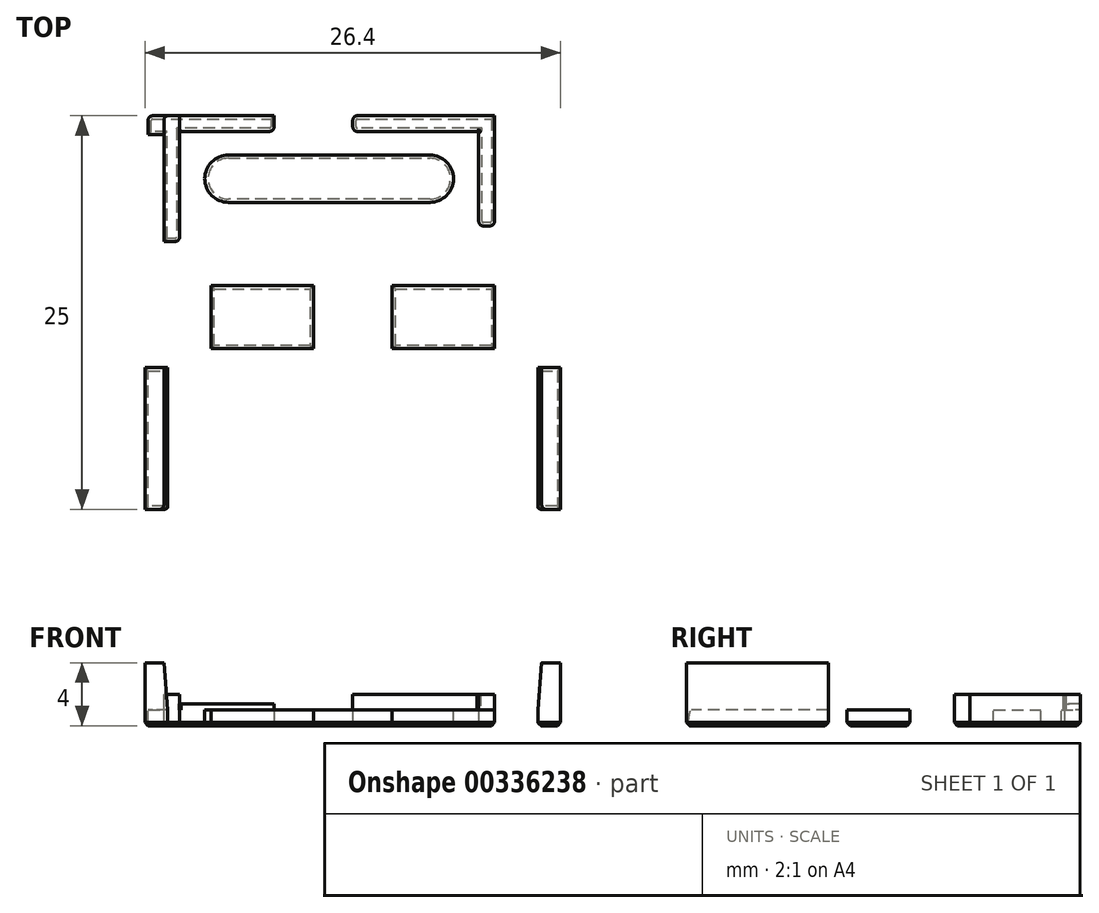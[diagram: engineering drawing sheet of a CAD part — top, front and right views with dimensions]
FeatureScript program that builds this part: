
annotation { "Feature Type Name" : "Feature", "Feature Type Description" : "" }
export const myFeature = defineFeature(function(context is Context, id is Id, definition is map)
    precondition{}
    {
        {
            var Q0;
            Q0=qCreatedBy(makeId("Top.planeOp"),FACE);
            var sketch = newSketch(context, id + "F0", { "sketchPlane" : qUnion([Q0])});
            skLineSegment(sketch, "E0.bottom", {"start": v(12, 8) * mm, "end": v(-12, 8) * mm, "construction": true});
            skLineSegment(sketch, "E0.top", {"start": v(12, -8) * mm, "end": v(-12, -8) * mm});
            skLineSegment(sketch, "E0.left", {"start": v(12, 8) * mm, "end": v(12, -8) * mm});
            skLineSegment(sketch, "E0.right", {"start": v(-12, 8) * mm, "end": v(-12, -8) * mm});
            skPoint(sketch, "E0.middle", {"position": v(0, 0) * mm});
            skLineSegment(sketch, "E1.bottom", {"start": v(-12, -8) * mm, "end": v(-13.2, -8) * mm});
            skLineSegment(sketch, "E1.top", {"start": v(-12, 1) * mm, "end": v(-13.2, 1) * mm});
            skLineSegment(sketch, "E1.right", {"start": v(-13.2, -8) * mm, "end": v(-13.2, 1) * mm});
            skLineSegment(sketch, "E2.bottom", {"start": v(12, -8) * mm, "end": v(13.2, -8) * mm});
            skLineSegment(sketch, "E2.top", {"start": v(12, 1) * mm, "end": v(13.2, 1) * mm});
            skLineSegment(sketch, "E2.right", {"start": v(13.2, -8) * mm, "end": v(13.2, 1) * mm});
            skLineSegment(sketch, "E3", {"start": v(-12, 8) * mm, "end": v(-12, 9) * mm});
            skLineSegment(sketch, "E4", {"start": v(-12, 9) * mm, "end": v(12, 9) * mm, "construction": true});
            skLineSegment(sketch, "E5", {"start": v(12, 9) * mm, "end": v(12, 8) * mm});
            skLineSegment(sketch, "E6", {"start": v(-12, 9) * mm, "end": v(-12, 17) * mm});
            skLineSegment(sketch, "E7", {"start": v(-12, 17) * mm, "end": v(12, 17) * mm});
            skLineSegment(sketch, "E8", {"start": v(12, 17) * mm, "end": v(12, 9) * mm});
            skSolve(sketch);
        }
        {
            var Q0;
            Q0=qCreatedBy(makeId("Front.planeOp"),FACE);
            var sketch = newSketch(context, id + "F1", { "sketchPlane" : qUnion([Q0])});
            skLineSegment(sketch, "E9", {"start": v(0, 0) * mm, "end": v(0, 1) * mm});
            skLineSegment(sketch, "E10", {"start": v(0, 1) * mm, "end": v(0, 4) * mm});
            skSolve(sketch);
        }
        {
            var Q0;
            {var subQ4=sQuery(id+"F0.wireOp",EDGE,"E0.top");Q0=makeQuery(id+"F0.imprint","IMPRINT",FACE,{"disambiguationData":[TD([[makeQuery(id+"F0.imprint","IMPRINT",EDGE,{"derivedFrom":subQ4}),-1.0]])]});}
            var Q1;
            {var subQ0=sQuery(id+"F0.wireOp",EDGE,"E1.bottom");Q1=makeQuery(id+"F0.imprint","IMPRINT",FACE,{"disambiguationData":[TD([[makeQuery(id+"F0.imprint","IMPRINT",EDGE,{"derivedFrom":subQ0}),-1.0]])]});}
            var Q2;
            {var subQ0=sQuery(id+"F0.wireOp",EDGE,"E2.bottom");Q2=makeQuery(id+"F0.imprint","IMPRINT",FACE,{"disambiguationData":[TD([[makeQuery(id+"F0.imprint","IMPRINT",EDGE,{"derivedFrom":subQ0}),1.0]])]});}
            var Q3;
            Q3=sQuery(id+"F1.wireOp",EDGE,"E9");
            sweep(context, id + "F2", {"profiles" : qUnion([Q0, Q1, Q2]), "path" : qUnion([Q3])});
        }
        {
            var Q0;
            {var subQ0=sQuery(id+"F0.wireOp",EDGE,"E1.bottom");Q0=makeQuery(id+"F0.imprint","IMPRINT",FACE,{"disambiguationData":[TD([[makeQuery(id+"F0.imprint","IMPRINT",EDGE,{"derivedFrom":subQ0}),-1.0]])]});}
            var Q1;
            {var subQ0=sQuery(id+"F0.wireOp",EDGE,"E2.bottom");Q1=makeQuery(id+"F0.imprint","IMPRINT",FACE,{"disambiguationData":[TD([[makeQuery(id+"F0.imprint","IMPRINT",EDGE,{"derivedFrom":subQ0}),1.0]])]});}
            var Q2;
            Q2=sQuery(id+"F1.wireOp",EDGE,"E9");
            var Q3;
            Q3=sQuery(id+"F1.wireOp",EDGE,"E10");
            sweep(context, id + "F3", {"operationType" : NewBodyOperationType.ADD, "profiles" : qUnion([Q0, Q1]), "path" : qUnion([Q2, Q3])});
        }
        {
            var Q0;
            {var subQ0=sQuery(id+"F1.wireOp",EDGE,"E9");var subQ1=sQuery(id+"F0.wireOp",EDGE,"E2.bottom");var subQ2=sQuery(id+"F0.wireOp",EDGE,"E1.bottom");Q0=makeQuery(id+"F3.boolean.opBoolean","MERGE",FACE,{"derivedFrom":[makeQuery(id+"F2.opSweep","SWEPT_FACE",FACE,{"disambiguationData":[OSD([sQuery(id+"F0.wireOp",EDGE,"E0.top"),subQ2,subQ1,subQ0])]}),makeQuery(id+"F3.opSweep","SWEPT_FACE",FACE,{"disambiguationData":[OSD([subQ2,subQ0])]}),makeQuery(id+"F3.opSweep","SWEPT_FACE",FACE,{"disambiguationData":[OSD([subQ1,subQ0])]})]});}
            var sketch = newSketch(context, id + "F4", { "sketchPlane" : qUnion([Q0])});
            skLineSegment(sketch, "E11", {"start": v(-12, 4) * mm, "end": v(-11.75, 1) * mm});
            skLineSegment(sketch, "E12", {"start": v(-11.75, 1) * mm, "end": v(-12, 1) * mm});
            skLineSegment(sketch, "E13", {"start": v(-12, 1) * mm, "end": v(-12, 4) * mm});
            skLineSegment(sketch, "E14.MirrorCS", {"start": v(12, 4) * mm, "end": v(11.75, 1) * mm});
            skLineSegment(sketch, "E15.MirrorCS", {"start": v(12, 1) * mm, "end": v(12, 4) * mm});
            skLineSegment(sketch, "E16.MirrorCS", {"start": v(11.75, 1) * mm, "end": v(12, 1) * mm});
            skSolve(sketch);
        }
        {
            var Q0;
            Q0 = qSketchRegion(id + "F4", true);
            var Q1;
            {var subQ0=sQuery(id+"F1.wireOp",EDGE,"E9");var subQ1=sQuery(id+"F0.wireOp",EDGE,"E1.top");Q1=makeQuery(id+"F3.boolean.opBoolean","MERGE",FACE,{"derivedFrom":[makeQuery(id+"F2.opSweep","SWEPT_FACE",FACE,{"disambiguationData":[OSD([subQ1,subQ0])]}),makeQuery(id+"F3.opSweep","SWEPT_FACE",FACE,{"disambiguationData":[OSD([subQ1,subQ0])]})]});}
            extrude(context, id + "F5", {"entities" : qUnion([Q0]), "operationType" : NewBodyOperationType.ADD, "endBound" : BoundingType.UP_TO_SURFACE, "oppositeDirection" : true, "depth" : 25 * mm, "endBoundEntityFace" : qUnion([Q1]), "offsetDistance" : 25 * mm});
        }
        {
            var Q0;
            Q0=makeQuery(id+"F2.opSweep","CAP_FACE",FACE,{"disambiguationData":[OSD([sQuery(id+"F0.wireOp",EDGE,"E0.top"),sQuery(id+"F0.wireOp",EDGE,"E0.left"),sQuery(id+"F0.wireOp",EDGE,"E0.right"),sQuery(id+"F0.wireOp",EDGE,"E1.bottom"),sQuery(id+"F0.wireOp",EDGE,"E1.top"),sQuery(id+"F0.wireOp",EDGE,"E1.right"),sQuery(id+"F0.wireOp",EDGE,"E2.bottom"),sQuery(id+"F0.wireOp",EDGE,"E2.top"),sQuery(id+"F0.wireOp",EDGE,"E2.right"),sQuery(id+"F0.wireOp",EDGE,"E3"),sQuery(id+"F0.wireOp",EDGE,"E5"),sQuery(id+"F0.wireOp",EDGE,"E6"),sQuery(id+"F0.wireOp",EDGE,"E7"),sQuery(id+"F0.wireOp",EDGE,"E8"),sQuery(id+"F1.wireOp",VERTEX,"E9.end")])],"isStart":false});
            var sketch = newSketch(context, id + "F6", { "sketchPlane" : qUnion([Q0])});
            skLineSegment(sketch, "E17.bottom", {"start": v(-12, 17) * mm, "end": v(-11, 17) * mm});
            skLineSegment(sketch, "E17.top", {"start": v(-12, 9) * mm, "end": v(-11, 9) * mm});
            skLineSegment(sketch, "E17.left", {"start": v(-12, 17) * mm, "end": v(-12, 9) * mm});
            skLineSegment(sketch, "E17.right", {"start": v(-11, 17) * mm, "end": v(-11, 9) * mm});
            skLineSegment(sketch, "E18", {"start": v(0, 17) * mm, "end": v(9, 17) * mm});
            skLineSegment(sketch, "E19", {"start": v(9, 17) * mm, "end": v(9, 10) * mm});
            skLineSegment(sketch, "E20", {"start": v(9, 10) * mm, "end": v(8, 10) * mm});
            skLineSegment(sketch, "E21", {"start": v(8, 10) * mm, "end": v(8, 16) * mm});
            skLineSegment(sketch, "E22", {"start": v(8, 16) * mm, "end": v(0, 16) * mm});
            skLineSegment(sketch, "E23", {"start": v(0, 16) * mm, "end": v(0, 17) * mm});
            skLineSegment(sketch, "E24", {"start": v(-7.9, 13) * mm, "end": v(4.9, 13) * mm, "construction": true});
            skPoint(sketch, "E24.startSnap0", {"position": v(-11, 13) * mm});
            skArc(sketch, "E25.0.startCap", {"start": v(-7.9, 11.5) * mm, "mid": v(-9.4, 13) * mm, "end": v(-7.9, 14.5) * mm});
            skArc(sketch, "E25.0.endCap", {"start": v(4.9, 14.5) * mm, "mid": v(6.4, 13) * mm, "end": v(4.9, 11.5) * mm});
            skLineSegment(sketch, "E25.0.left", {"start": v(-7.9, 14.5) * mm, "end": v(4.9, 14.5) * mm});
            skLineSegment(sketch, "E25.0.right", {"start": v(-7.9, 11.5) * mm, "end": v(4.9, 11.5) * mm});
            skLineSegment(sketch, "E26", {"start": v(8, 10) * mm, "end": v(-11, 10) * mm, "construction": true});
            skArc(sketch, "E27", {"start": v(12, 14.5) * mm, "mid": v(10.5, 13) * mm, "end": v(12, 11.5) * mm});
            skLineSegment(sketch, "E28", {"start": v(12, 14.5) * mm, "end": v(12, 11.5) * mm});
            skLineSegment(sketch, "E29", {"start": v(-12, 17) * mm, "end": v(-13, 17) * mm});
            skLineSegment(sketch, "E30", {"start": v(-13, 17) * mm, "end": v(-13, 15.8) * mm});
            skLineSegment(sketch, "E31", {"start": v(-13, 15.8) * mm, "end": v(-12, 15.8) * mm});
            skLineSegment(sketch, "E32.bottom", {"start": v(-2.5, 6.2) * mm, "end": v(-9, 6.2) * mm});
            skLineSegment(sketch, "E32.top", {"start": v(-2.5, 2.2) * mm, "end": v(-9, 2.2) * mm});
            skLineSegment(sketch, "E32.left", {"start": v(-2.5, 6.2) * mm, "end": v(-2.5, 2.2) * mm});
            skLineSegment(sketch, "E32.right", {"start": v(-9, 6.2) * mm, "end": v(-9, 2.2) * mm});
            skLineSegment(sketch, "E33.MirrorCS", {"start": v(2.5, 6.2) * mm, "end": v(2.5, 2.2) * mm});
            skLineSegment(sketch, "E34.MirrorCS", {"start": v(2.5, 6.2) * mm, "end": v(9, 6.2) * mm});
            skLineSegment(sketch, "E35.MirrorCS", {"start": v(2.5, 2.2) * mm, "end": v(9, 2.2) * mm});
            skLineSegment(sketch, "E36.MirrorCS", {"start": v(9, 6.2) * mm, "end": v(9, 2.2) * mm});
            skLineSegment(sketch, "E37", {"start": v(-11, 17) * mm, "end": v(-5, 17) * mm});
            skLineSegment(sketch, "E38", {"start": v(-5, 17) * mm, "end": v(-5, 16) * mm});
            skLineSegment(sketch, "E39", {"start": v(-5, 16) * mm, "end": v(-11, 16) * mm});
            skSolve(sketch);
        }
        {
            var Q0;
            {var subQ1=sQuery(id+"F6.wireOp",EDGE,"E17.bottom");Q0=makeQuery(id+"F6.imprint","IMPRINT",FACE,{"disambiguationData":[TD([[makeQuery(id+"F6.imprint","IMPRINT",EDGE,{"derivedFrom":subQ1}),1.0]])]});}
            var Q1;
            Q1=makeQuery(id+"F6.imprint","IMPRINT",FACE,{"disambiguationData":[TD([[makeQuery(id+"F6.imprint","IMPRINT",EDGE,{"derivedFrom":sQuery(id+"F6.wireOp",EDGE,"E18")}),1.0]])]});
            extrude(context, id + "F7", {"entities" : qUnion([Q0, Q1]), "operationType" : NewBodyOperationType.ADD, "depth" : 1 * mm, "offsetDistance" : 25 * mm});
        }
        {
            var Q0;
            {var subQ0=sQuery(id+"F6.wireOp",EDGE,"E37");Q0=makeQuery(id+"F6.imprint","IMPRINT",FACE,{"disambiguationData":[TD([[makeQuery(id+"F6.imprint","IMPRINT",EDGE,{"derivedFrom":subQ0}),1.0]])]});}
            extrude(context, id + "F8", {"entities" : qUnion([Q0]), "operationType" : NewBodyOperationType.ADD, "depth" : 0.4 * mm, "offsetDistance" : 25 * mm});
        }
        {
            var Q0;
            Q0=makeQuery(id+"F6.imprint","IMPRINT",FACE,{"disambiguationData":[TD([[makeQuery(id+"F6.imprint","IMPRINT",EDGE,{"derivedFrom":sQuery(id+"F6.wireOp",EDGE,"E25.0.startCap")}),-1.0]])]});
            var Q1;
            Q1=makeQuery(id+"F6.imprint","IMPRINT",FACE,{"disambiguationData":[TD([[makeQuery(id+"F6.imprint","IMPRINT",EDGE,{"derivedFrom":sQuery(id+"F6.wireOp",EDGE,"E27")}),1.0]])]});
            var Q2;
            Q2=makeQuery(id+"F2.opSweep","CAP_FACE",FACE,{"disambiguationData":[OSD([sQuery(id+"F0.wireOp",EDGE,"E0.top"),sQuery(id+"F0.wireOp",EDGE,"E0.left"),sQuery(id+"F0.wireOp",EDGE,"E0.right"),sQuery(id+"F0.wireOp",EDGE,"E1.bottom"),sQuery(id+"F0.wireOp",EDGE,"E1.top"),sQuery(id+"F0.wireOp",EDGE,"E1.right"),sQuery(id+"F0.wireOp",EDGE,"E2.bottom"),sQuery(id+"F0.wireOp",EDGE,"E2.top"),sQuery(id+"F0.wireOp",EDGE,"E2.right"),sQuery(id+"F0.wireOp",EDGE,"E3"),sQuery(id+"F0.wireOp",EDGE,"E5"),sQuery(id+"F0.wireOp",EDGE,"E6"),sQuery(id+"F0.wireOp",EDGE,"E7"),sQuery(id+"F0.wireOp",EDGE,"E8"),sQuery(id+"F1.wireOp",VERTEX,"E9.start")])],"isStart":true});
            extrude(context, id + "F9", {"entities" : qUnion([Q0, Q1]), "operationType" : NewBodyOperationType.REMOVE, "endBound" : BoundingType.UP_TO_SURFACE, "oppositeDirection" : true, "depth" : 25 * mm, "endBoundEntityFace" : qUnion([Q2]), "offsetDistance" : 25 * mm});
        }
        {
            var Q0;
            {var subQ0=sQuery(id+"F6.wireOp",EDGE,"E29");Q0=makeQuery(id+"F6.imprint","IMPRINT",FACE,{"disambiguationData":[TD([[makeQuery(id+"F6.imprint","IMPRINT",EDGE,{"derivedFrom":subQ0}),1.0]])]});}
            var Q1;
            Q1=makeQuery(id+"F2.opSweep","CAP_FACE",FACE,{"disambiguationData":[OSD([sQuery(id+"F0.wireOp",EDGE,"E0.top"),sQuery(id+"F0.wireOp",EDGE,"E0.left"),sQuery(id+"F0.wireOp",EDGE,"E0.right"),sQuery(id+"F0.wireOp",EDGE,"E1.bottom"),sQuery(id+"F0.wireOp",EDGE,"E1.top"),sQuery(id+"F0.wireOp",EDGE,"E1.right"),sQuery(id+"F0.wireOp",EDGE,"E2.bottom"),sQuery(id+"F0.wireOp",EDGE,"E2.top"),sQuery(id+"F0.wireOp",EDGE,"E2.right"),sQuery(id+"F0.wireOp",EDGE,"E3"),sQuery(id+"F0.wireOp",EDGE,"E5"),sQuery(id+"F0.wireOp",EDGE,"E6"),sQuery(id+"F0.wireOp",EDGE,"E7"),sQuery(id+"F0.wireOp",EDGE,"E8"),sQuery(id+"F1.wireOp",VERTEX,"E9.start")])],"isStart":true});
            extrude(context, id + "F10", {"entities" : qUnion([Q0]), "operationType" : NewBodyOperationType.ADD, "endBound" : BoundingType.UP_TO_SURFACE, "oppositeDirection" : true, "depth" : 25 * mm, "endBoundEntityFace" : qUnion([Q1]), "offsetDistance" : 25 * mm});
        }
        {
            var Q0;
            Q0=makeQuery(id+"F5.opExtrude","CAP_EDGE",EDGE,{"disambiguationData":[OSD([sQuery(id+"F4.wireOp",EDGE,"E11")])],"isStart":true});
            var Q1;
            {var subQ0=sQuery(id+"F1.wireOp",EDGE,"E9");var subQ1=sQuery(id+"F0.wireOp",EDGE,"E1.top");Q1=makeQuery(id+"F5.opExtrude","TWEAK_EDGE",EDGE,{"derivedFrom":[makeQuery(id+"F3.boolean.opBoolean","MERGE",FACE,{"derivedFrom":[makeQuery(id+"F2.opSweep","SWEPT_FACE",FACE,{"disambiguationData":[OSD([subQ1,subQ0])]}),makeQuery(id+"F3.opSweep","SWEPT_FACE",FACE,{"disambiguationData":[OSD([subQ1,subQ0])]})]}),makeQuery(id+"F4.imprint","IMPRINT",EDGE,{"derivedFrom":sQuery(id+"F4.wireOp",EDGE,"E11")})]});}
            var Q2;
            {var subQ0=sQuery(id+"F1.wireOp",EDGE,"E9");var subQ1=sQuery(id+"F0.wireOp",EDGE,"E1.top");Q2=makeQuery(id+"F5.opExtrude","TWEAK_EDGE",EDGE,{"derivedFrom":[makeQuery(id+"F3.boolean.opBoolean","MERGE",FACE,{"derivedFrom":[makeQuery(id+"F2.opSweep","SWEPT_FACE",FACE,{"disambiguationData":[OSD([subQ1,subQ0])]}),makeQuery(id+"F3.opSweep","SWEPT_FACE",FACE,{"disambiguationData":[OSD([subQ1,subQ0])]})]}),makeQuery(id+"F4.imprint","IMPRINT",EDGE,{"derivedFrom":sQuery(id+"F4.wireOp",EDGE,"E14.MirrorCS")})]});}
            var Q3;
            Q3=makeQuery(id+"F5.opExtrude","CAP_EDGE",EDGE,{"disambiguationData":[OSD([sQuery(id+"F4.wireOp",EDGE,"E14.MirrorCS")])],"isStart":true});
            var Q4;
            Q4=makeQuery(id+"F7.opExtrude","SWEPT_EDGE",EDGE,{"disambiguationData":[OSD([sQuery(id+"F6.wireOp",EDGE,"E17.top"),sQuery(id+"F6.wireOp",EDGE,"E17.right")])]});
            var Q5;
            Q5=makeQuery(id+"F7.opExtrude","SWEPT_EDGE",EDGE,{"disambiguationData":[OSD([sQuery(id+"F6.wireOp",EDGE,"E22"),sQuery(id+"F6.wireOp",EDGE,"E23")])]});
            var Q6;
            Q6=makeQuery(id+"F7.opExtrude","SWEPT_EDGE",EDGE,{"disambiguationData":[OSD([sQuery(id+"F0.wireOp",EDGE,"E7"),sQuery(id+"F1.wireOp",VERTEX,"E9.end"),sQuery(id+"F6.wireOp",EDGE,"E18"),sQuery(id+"F6.wireOp",EDGE,"E23")])]});
            var Q7;
            Q7=makeQuery(id+"F7.opExtrude","SWEPT_EDGE",EDGE,{"disambiguationData":[OSD([sQuery(id+"F6.wireOp",EDGE,"E20"),sQuery(id+"F6.wireOp",EDGE,"E21")])]});
            var Q8;
            Q8=makeQuery(id+"F7.opExtrude","SWEPT_EDGE",EDGE,{"disambiguationData":[OSD([sQuery(id+"F6.wireOp",EDGE,"E19"),sQuery(id+"F6.wireOp",EDGE,"E20")])]});
            var Q9;
            Q9=makeQuery(id+"F7.opExtrude","SWEPT_EDGE",EDGE,{"disambiguationData":[OSD([sQuery(id+"F0.wireOp",EDGE,"E0.right"),sQuery(id+"F0.wireOp",EDGE,"E3"),sQuery(id+"F0.wireOp",EDGE,"E6"),sQuery(id+"F1.wireOp",VERTEX,"E9.end"),sQuery(id+"F6.wireOp",EDGE,"E17.top"),sQuery(id+"F6.wireOp",EDGE,"E17.left")])]});
            var Q10;
            Q10=makeQuery(id+"F7.boolean.opBoolean","MERGE",EDGE,{"derivedFrom":[makeQuery(id+"F2.opSweep","SWEPT_EDGE",EDGE,{"disambiguationData":[OSD([sQuery(id+"F0.wireOp",EDGE,"E6"),sQuery(id+"F0.wireOp",EDGE,"E7"),sQuery(id+"F1.wireOp",EDGE,"E9")])]}),makeQuery(id+"F7.opExtrude","SWEPT_EDGE",EDGE,{"disambiguationData":[OSD([sQuery(id+"F6.wireOp",EDGE,"E17.bottom"),sQuery(id+"F6.wireOp",EDGE,"E17.left"),sQuery(id+"F6.wireOp",EDGE,"E29")])]})]});
            var Q11;
            Q11=makeQuery(id+"F10.opExtrude","SWEPT_EDGE",EDGE,{"disambiguationData":[OSD([sQuery(id+"F6.wireOp",EDGE,"E29"),sQuery(id+"F6.wireOp",EDGE,"E30")])]});
            var Q12;
            Q12=makeQuery(id+"F8.opExtrude","SWEPT_EDGE",EDGE,{"disambiguationData":[OSD([sQuery(id+"F6.wireOp",EDGE,"E38"),sQuery(id+"F6.wireOp",EDGE,"E39")])]});
            var Q13;
            Q13=makeQuery(id+"F8.opExtrude","SWEPT_EDGE",EDGE,{"disambiguationData":[OSD([sQuery(id+"F0.wireOp",EDGE,"E7"),sQuery(id+"F1.wireOp",VERTEX,"E9.end"),sQuery(id+"F6.wireOp",EDGE,"E37"),sQuery(id+"F6.wireOp",EDGE,"E38")])]});
            fillet(context, id + "F11", {"entities" : qUnion([Q0, Q1, Q2, Q3, Q4, Q5, Q6, Q7, Q8, Q9, Q10, Q11, Q12, Q13]), "radius" : .3 * mm, "allowEdgeOverflow" : false});
        }
        {
            var Q0;
            {var subQ5=sQuery(id+"F6.wireOp",EDGE,"E17.top");Q0=makeQuery(id+"F6.imprint","IMPRINT",FACE,{"disambiguationData":[TD([[makeQuery(id+"F6.imprint","IMPRINT",EDGE,{"derivedFrom":subQ5}),-1.0]])]});}
            var sketch = newSketch(context, id + "F12", { "sketchPlane" : qUnion([Q0])});
            skCircle(sketch, "E40", {"center": v(8, 16) * mm, "radius": 0.1 * mm});
            skPoint(sketch, "E41.0", {"position": v(-11, 16) * mm});
            skCircle(sketch, "E42", {"center": v(-11, 16) * mm, "radius": 0.1 * mm});
            skSolve(sketch);
        }
        {
            var Q0;
            {var subQ0=sQuery(id+"F12.wireOp",EDGE,"E40");var subQ1=makeQuery(id+"F7.opExtrude","CAP_EDGE",EDGE,{"disambiguationData":[OSD([sQuery(id+"F6.wireOp",EDGE,"E21")])],"isStart":false});var subQ2=makeQuery(id+"F12.imprint","INTERSECT",VERTEX,{"derivedFrom":[subQ1,subQ0]});Q0=makeQuery(id+"F12.imprint","IMPRINT",FACE,{"disambiguationData":[TD([[makeQuery(id+"F12.imprint","IMPRINT",EDGE,{"disambiguationData":[TD([[subQ2,-1.0]])],"derivedFrom":subQ0}),1.0]])]});}
            var Q1;
            Q1=makeQuery(id+"F7.opExtrude","CAP_FACE",FACE,{"disambiguationData":[OSD([sQuery(id+"F6.wireOp",EDGE,"E18"),sQuery(id+"F6.wireOp",EDGE,"E19"),sQuery(id+"F6.wireOp",EDGE,"E20"),sQuery(id+"F6.wireOp",EDGE,"E21"),sQuery(id+"F6.wireOp",EDGE,"E22"),sQuery(id+"F6.wireOp",EDGE,"E23")])],"isStart":false});
            extrude(context, id + "F13", {"entities" : qUnion([Q0]), "operationType" : NewBodyOperationType.REMOVE, "endBound" : BoundingType.UP_TO_SURFACE, "depth" : 25 * mm, "endBoundEntityFace" : qUnion([Q1]), "offsetDistance" : 25 * mm});
        }
        {
            var Q0;
            {var subQ0=sQuery(id+"F12.wireOp",EDGE,"E42");var subQ2=sQuery(id+"F6.wireOp",EDGE,"E39");var subQ5=makeQuery(id+"F6.imprint","IMPRINT",EDGE,{"derivedFrom":subQ2});var subQ6=makeQuery(id+"F12.imprint","INTERSECT",VERTEX,{"derivedFrom":[subQ5,subQ0]});Q0=makeQuery(id+"F12.imprint","IMPRINT",FACE,{"disambiguationData":[TD([[makeQuery(id+"F12.imprint","IMPRINT",EDGE,{"disambiguationData":[TD([[subQ6,-1.0]])],"derivedFrom":subQ0}),1.0]])]});}
            var Q1;
            Q1=makeQuery(id+"F8.opExtrude","CAP_FACE",FACE,{"disambiguationData":[OSD([sQuery(id+"F6.wireOp",EDGE,"E17.right"),sQuery(id+"F6.wireOp",EDGE,"E37"),sQuery(id+"F6.wireOp",EDGE,"E38"),sQuery(id+"F6.wireOp",EDGE,"E39")])],"isStart":false});
            extrude(context, id + "F14", {"entities" : qUnion([Q0]), "operationType" : NewBodyOperationType.REMOVE, "endBound" : BoundingType.UP_TO_SURFACE, "depth" : 25 * mm, "endBoundEntityFace" : qUnion([Q1]), "offsetDistance" : 25 * mm});
        }
        {
            var Q0;
            Q0=makeQuery(id+"F2.opSweep","CAP_FACE",FACE,{"disambiguationData":[OSD([sQuery(id+"F0.wireOp",EDGE,"E0.top"),sQuery(id+"F0.wireOp",EDGE,"E0.left"),sQuery(id+"F0.wireOp",EDGE,"E0.right"),sQuery(id+"F0.wireOp",EDGE,"E1.bottom"),sQuery(id+"F0.wireOp",EDGE,"E1.top"),sQuery(id+"F0.wireOp",EDGE,"E1.right"),sQuery(id+"F0.wireOp",EDGE,"E2.bottom"),sQuery(id+"F0.wireOp",EDGE,"E2.top"),sQuery(id+"F0.wireOp",EDGE,"E2.right"),sQuery(id+"F0.wireOp",EDGE,"E3"),sQuery(id+"F0.wireOp",EDGE,"E5"),sQuery(id+"F0.wireOp",EDGE,"E6"),sQuery(id+"F0.wireOp",EDGE,"E7"),sQuery(id+"F0.wireOp",EDGE,"E8"),sQuery(id+"F1.wireOp",VERTEX,"E9.start")])],"isStart":true});
            chamfer(context, id + "F15", {"entities" : qUnion([Q0]), "width" : .2 * mm});
        }
    });
